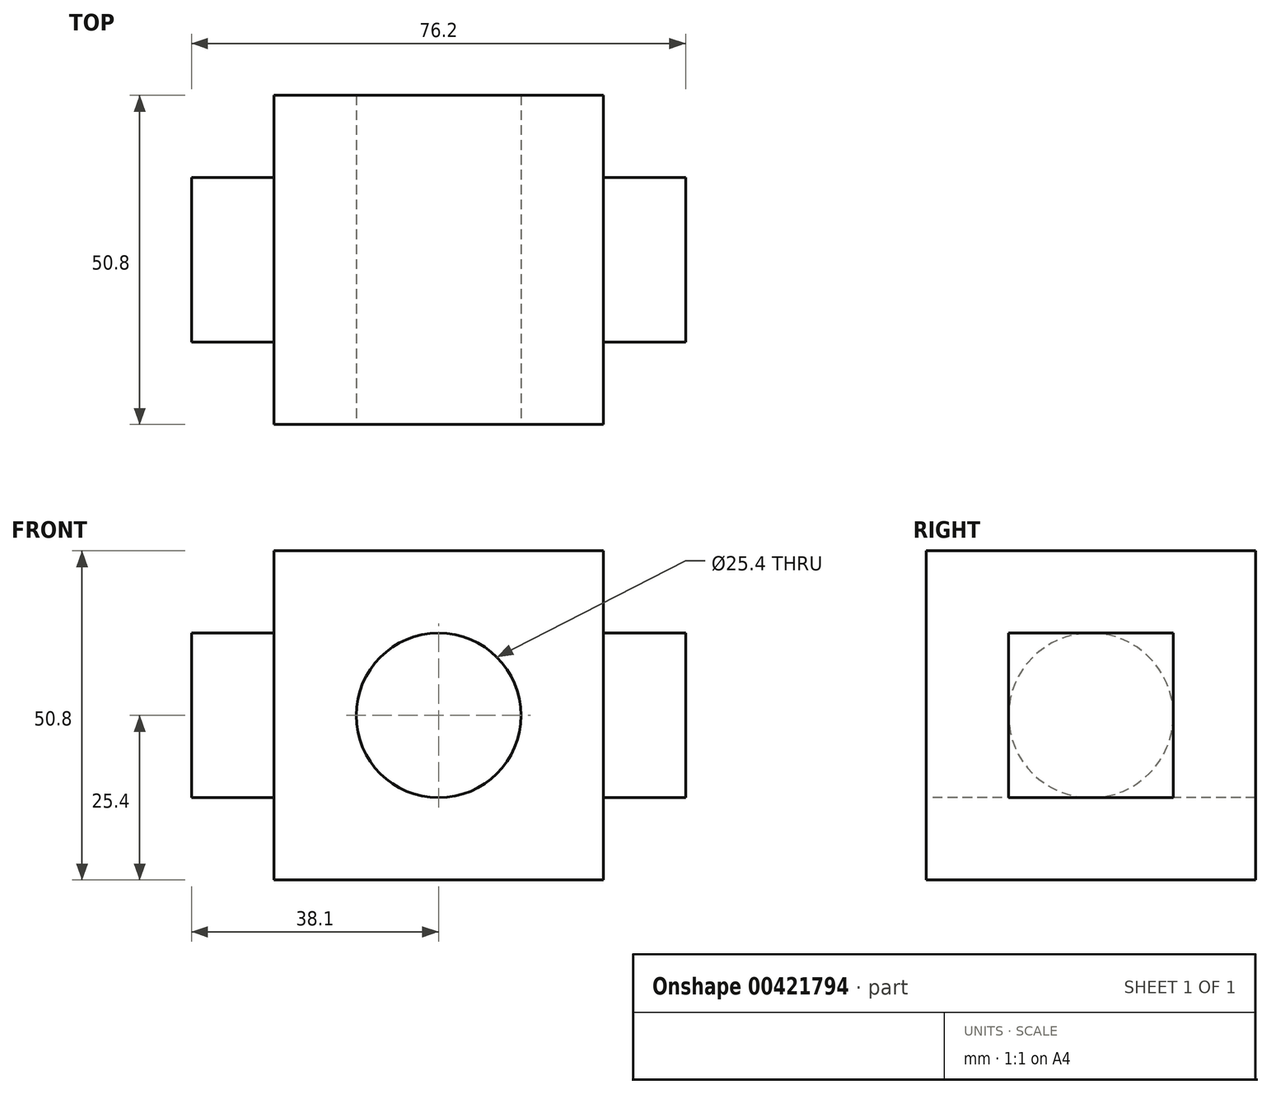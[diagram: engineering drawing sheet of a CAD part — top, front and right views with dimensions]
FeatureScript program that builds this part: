
annotation { "Feature Type Name" : "Feature", "Feature Type Description" : "" }
export const myFeature = defineFeature(function(context is Context, id is Id, definition is map)
    precondition{}
    {
        {
            var Q0;
            Q0=qCreatedBy(makeId("Front.planeOp"),FACE);
            var sketch = newSketch(context, id + "F0", { "sketchPlane" : qUnion([Q0])});
            skLineSegment(sketch, "E0.bottom", {"start": v(0, 0) * mm, "end": v(50.8, 0) * mm});
            skLineSegment(sketch, "E0.top", {"start": v(0, 50.8) * mm, "end": v(50.8, 50.8) * mm});
            skLineSegment(sketch, "E0.left", {"start": v(0, 0) * mm, "end": v(0, 50.8) * mm});
            skLineSegment(sketch, "E0.right", {"start": v(50.8, 0) * mm, "end": v(50.8, 50.8) * mm});
            skSolve(sketch);
        }
        {
            var Q0;
            Q0=makeQuery(id+"F0.imprint","IMPRINT",FACE,{"disambiguationData":[TD([[makeQuery(id+"F0.imprint","IMPRINT",EDGE,{"derivedFrom":sQuery(id+"F0.wireOp",EDGE,"E0.bottom")}),1.0]])]});
            extrude(context, id + "F1", {"entities" : qUnion([Q0]), "depth" : 50.8 * mm});
        }
        {
            var Q0;
            Q0=makeQuery(id+"F1.opExtrude","CAP_FACE",FACE,{"disambiguationData":[OSD([sQuery(id+"F0.wireOp",EDGE,"E0.bottom"),sQuery(id+"F0.wireOp",EDGE,"E0.top"),sQuery(id+"F0.wireOp",EDGE,"E0.left"),sQuery(id+"F0.wireOp",EDGE,"E0.right")])],"isStart":false});
            var sketch = newSketch(context, id + "F2", { "sketchPlane" : qUnion([Q0])});
            skCircle(sketch, "E1", {"center": v(25.4, 25.4) * mm, "radius": 12.7 * mm});
            skSolve(sketch);
        }
        {
            var Q0;
            Q0=makeQuery(id+"F2.imprint","IMPRINT",FACE,{"disambiguationData":[TD([[makeQuery(id+"F2.imprint","IMPRINT",EDGE,{"derivedFrom":sQuery(id+"F2.wireOp",EDGE,"E1")}),1.0]])]});
            extrude(context, id + "F3", {"entities" : qUnion([Q0]), "operationType" : NewBodyOperationType.REMOVE, "oppositeDirection" : true, "depth" : 50.8 * mm});
        }
        {
            var Q0;
            Q0=makeQuery(id+"F1.opExtrude","SWEPT_FACE",FACE,{"disambiguationData":[OSD([sQuery(id+"F0.wireOp",EDGE,"E0.right")])]});
            var sketch = newSketch(context, id + "F4", { "sketchPlane" : qUnion([Q0])});
            skLineSegment(sketch, "E2.bottom", {"start": v(-38.1, 38.1) * mm, "end": v(-12.7, 38.1) * mm});
            skLineSegment(sketch, "E2.top", {"start": v(-38.1, 12.7) * mm, "end": v(-12.7, 12.7) * mm});
            skLineSegment(sketch, "E2.left", {"start": v(-38.1, 38.1) * mm, "end": v(-38.1, 12.7) * mm});
            skLineSegment(sketch, "E2.right", {"start": v(-12.7, 38.1) * mm, "end": v(-12.7, 12.7) * mm});
            skSolve(sketch);
        }
        {
            var Q0;
            Q0=makeQuery(id+"F4.imprint","IMPRINT",FACE,{"disambiguationData":[TD([[makeQuery(id+"F4.imprint","IMPRINT",EDGE,{"derivedFrom":sQuery(id+"F4.wireOp",EDGE,"E2.bottom")}),-1.0]])]});
            extrude(context, id + "F5", {"entities" : qUnion([Q0]), "operationType" : NewBodyOperationType.ADD, "depth" : 12.7 * mm});
        }
        {
            var Q0;
            Q0=makeQuery(id+"F1.opExtrude","SWEPT_FACE",FACE,{"disambiguationData":[OSD([sQuery(id+"F0.wireOp",EDGE,"E0.left")])]});
            var sketch = newSketch(context, id + "F6", { "sketchPlane" : qUnion([Q0])});
            skCircle(sketch, "E3", {"center": v(25.4, 25.4) * mm, "radius": 12.7 * mm});
            skSolve(sketch);
        }
        {
            var Q0;
            Q0=makeQuery(id+"F6.imprint","IMPRINT",FACE,{"disambiguationData":[TD([[makeQuery(id+"F6.imprint","IMPRINT",EDGE,{"derivedFrom":sQuery(id+"F6.wireOp",EDGE,"E3")}),1.0]])]});
            extrude(context, id + "F7", {"entities" : qUnion([Q0]), "operationType" : NewBodyOperationType.ADD, "depth" : 12.7 * mm});
        }
    });
